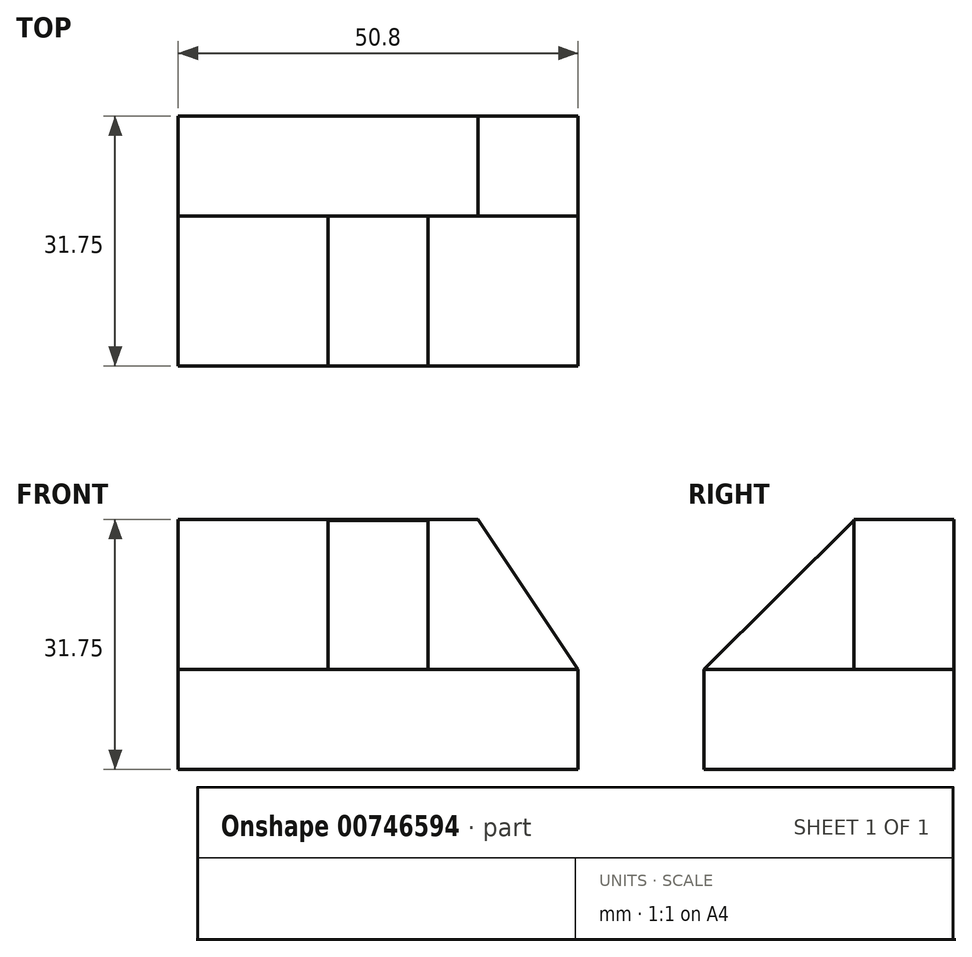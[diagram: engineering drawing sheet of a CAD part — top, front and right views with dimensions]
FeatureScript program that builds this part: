
annotation { "Feature Type Name" : "Feature", "Feature Type Description" : "" }
export const myFeature = defineFeature(function(context is Context, id is Id, definition is map)
    precondition{}
    {
        {
            var Q0;
            Q0=qCreatedBy(makeId("Front.planeOp"),FACE);
            var sketch = newSketch(context, id + "F0", { "sketchPlane" : qUnion([Q0])});
            skLineSegment(sketch, "E0.bottom", {"start": v(0, 0) * mm, "end": v(50.8, 0) * mm});
            skLineSegment(sketch, "E0.top", {"start": v(0, 31.75) * mm, "end": v(50.8, 31.75) * mm});
            skLineSegment(sketch, "E0.left", {"start": v(0, 0) * mm, "end": v(0, 31.75) * mm});
            skLineSegment(sketch, "E0.right", {"start": v(50.8, 0) * mm, "end": v(50.8, 31.75) * mm});
            skSolve(sketch);
        }
        {
            var Q0;
            Q0=makeQuery(id+"F0.imprint","IMPRINT",FACE,{"disambiguationData":[TD([[makeQuery(id+"F0.imprint","IMPRINT",EDGE,{"derivedFrom":sQuery(id+"F0.wireOp",EDGE,"E0.bottom")}),1.0]])]});
            extrude(context, id + "F1", {"entities" : qUnion([Q0]), "depth" : 31.75 * mm, "offsetDistance" : 25.4 * mm});
        }
        {
            var Q0;
            Q0=makeQuery(id+"F1.opExtrude","SWEPT_FACE",FACE,{"disambiguationData":[OSD([sQuery(id+"F0.wireOp",EDGE,"E0.right")])]});
            var sketch = newSketch(context, id + "F2", { "sketchPlane" : qUnion([Q0])});
            skLineSegment(sketch, "E1.bottom", {"start": v(-31.75, 31.75) * mm, "end": v(-12.7, 31.75) * mm});
            skLineSegment(sketch, "E1.top", {"start": v(-31.75, 12.7) * mm, "end": v(-12.7, 12.7) * mm});
            skLineSegment(sketch, "E1.left", {"start": v(-31.75, 31.75) * mm, "end": v(-31.75, 12.7) * mm});
            skLineSegment(sketch, "E1.right", {"start": v(-12.7, 31.75) * mm, "end": v(-12.7, 12.7) * mm});
            skSolve(sketch);
        }
        {
            var Q0;
            Q0=makeQuery(id+"F2.imprint","IMPRINT",FACE,{"disambiguationData":[TD([[makeQuery(id+"F2.imprint","IMPRINT",EDGE,{"derivedFrom":sQuery(id+"F2.wireOp",EDGE,"E1.bottom")}),-1.0]])]});
            extrude(context, id + "F3", {"entities" : qUnion([Q0]), "operationType" : NewBodyOperationType.REMOVE, "oppositeDirection" : true, "depth" : 50.8 * mm, "offsetDistance" : 25.4 * mm});
        }
        {
            var Q0;
            Q0=makeQuery(id+"F3.boolean.opBoolean","COPY",FACE,{"derivedFrom":makeQuery(id+"F3.opExtrude","SWEPT_FACE",FACE,{"disambiguationData":[OSD([sQuery(id+"F2.wireOp",EDGE,"E1.right")])]})});
            var sketch = newSketch(context, id + "F4", { "sketchPlane" : qUnion([Q0])});
            skLineSegment(sketch, "E2", {"start": v(50.8, 12.7) * mm, "end": v(50.8, 31.75) * mm});
            skLineSegment(sketch, "E3", {"start": v(50.8, 31.75) * mm, "end": v(38.1, 31.75) * mm});
            skLineSegment(sketch, "E4", {"start": v(38.1, 31.75) * mm, "end": v(50.8, 12.7) * mm});
            skSolve(sketch);
        }
        {
            var Q0;
            Q0=makeQuery(id+"F4.imprint","IMPRINT",FACE,{"disambiguationData":[TD([[makeQuery(id+"F4.imprint","IMPRINT",EDGE,{"derivedFrom":sQuery(id+"F4.wireOp",EDGE,"E2")}),-1.0]])]});
            extrude(context, id + "F5", {"entities" : qUnion([Q0]), "operationType" : NewBodyOperationType.REMOVE, "oppositeDirection" : true, "depth" : 12.7 * mm, "offsetDistance" : 25.4 * mm});
        }
        {
            var Q0;
            Q0=makeQuery(id+"F1.opExtrude","SWEPT_FACE",FACE,{"disambiguationData":[OSD([sQuery(id+"F0.wireOp",EDGE,"E0.right")])]});
            var sketch = newSketch(context, id + "F6", { "sketchPlane" : qUnion([Q0])});
            skLineSegment(sketch, "E5", {"start": v(-31.75, 12.7) * mm, "end": v(-12.7, 12.7) * mm});
            skLineSegment(sketch, "E6", {"start": v(-12.7, 12.7) * mm, "end": v(-12.7, 31.64) * mm});
            skLineSegment(sketch, "E7", {"start": v(-12.7, 31.64) * mm, "end": v(-31.75, 12.7) * mm});
            skSolve(sketch);
        }
        {
            var Q0;
            Q0=makeQuery(id+"F6.imprint","IMPRINT",FACE,{"disambiguationData":[TD([[makeQuery(id+"F6.imprint","IMPRINT",EDGE,{"derivedFrom":sQuery(id+"F6.wireOp",EDGE,"E5")}),1.0]])]});
            extrude(context, id + "F7", {"entities" : qUnion([Q0]), "operationType" : NewBodyOperationType.ADD, "oppositeDirection" : true, "depth" : 31.75 * mm, "offsetDistance" : 25.4 * mm, "hasSecondDirection" : true, "secondDirectionOppositeDirection" : true, "secondDirectionDepth" : 19.05 * mm});
        }
    });
